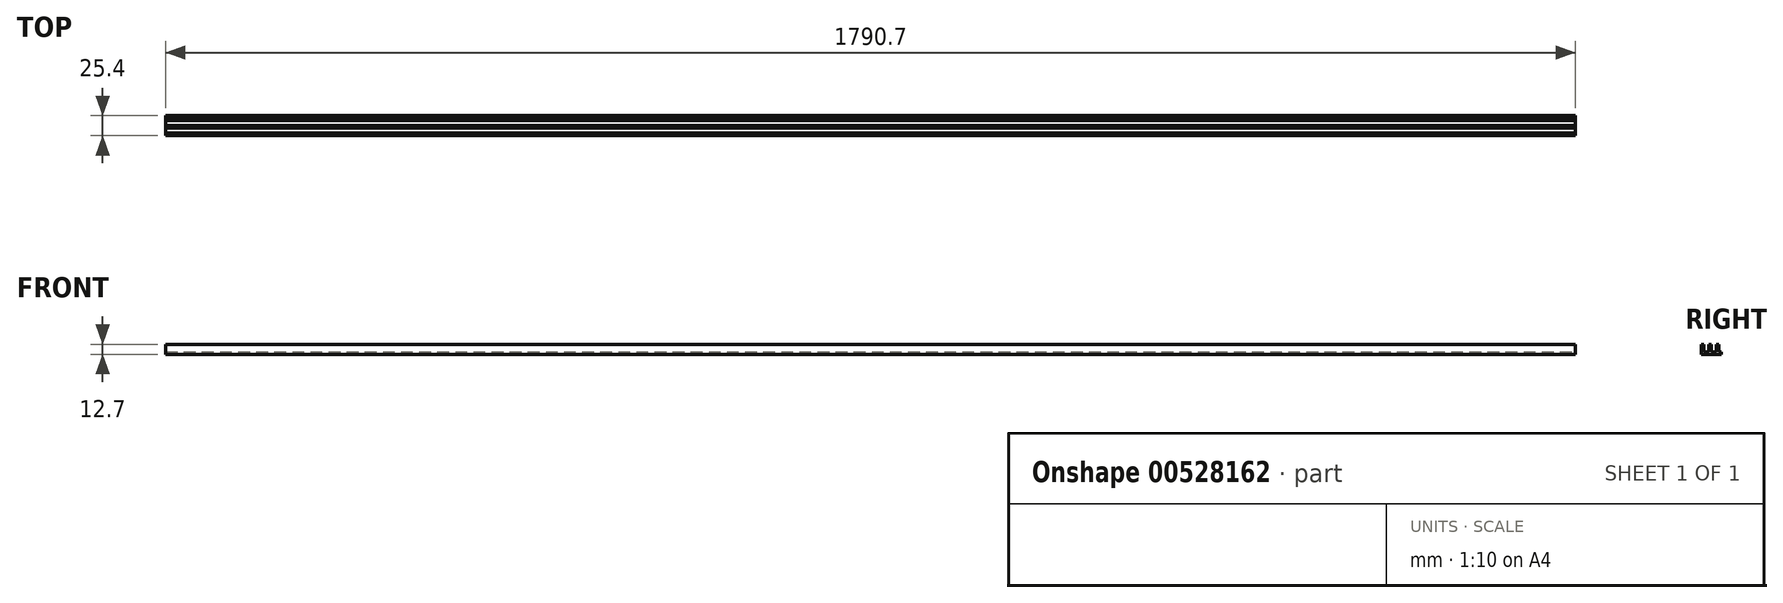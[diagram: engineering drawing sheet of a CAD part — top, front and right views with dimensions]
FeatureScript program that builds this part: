
annotation { "Feature Type Name" : "Feature", "Feature Type Description" : "" }
export const myFeature = defineFeature(function(context is Context, id is Id, definition is map)
    precondition{}
    {
        {
            var Q0;
            Q0=qCreatedBy(makeId("Top.planeOp"),FACE);
            var sketch = newSketch(context, id + "F0", { "sketchPlane" : qUnion([Q0])});
            skLineSegment(sketch, "E0.bottom", {"start": v(895.35, -12.7) * mm, "end": v(-895.35, -12.7) * mm});
            skLineSegment(sketch, "E0.top", {"start": v(895.35, 12.7) * mm, "end": v(-895.35, 12.7) * mm});
            skLineSegment(sketch, "E0.left", {"start": v(895.35, -12.7) * mm, "end": v(895.35, 12.7) * mm});
            skLineSegment(sketch, "E0.right", {"start": v(-895.35, -12.7) * mm, "end": v(-895.35, 12.7) * mm});
            skPoint(sketch, "E0.middle", {"position": v(0, 0) * mm});
            skSolve(sketch);
        }
        {
            var Q0;
            Q0=makeQuery(id+"F0.imprint","IMPRINT",FACE,{"disambiguationData":[TD([[makeQuery(id+"F0.imprint","IMPRINT",EDGE,{"derivedFrom":sQuery(id+"F0.wireOp",EDGE,"E0.bottom")}),-1.0]])]});
            extrude(context, id + "F1", {"entities" : qUnion([Q0]), "depth" : 3.17 * mm, "offsetDistance" : 25.4 * mm});
        }
        {
            var Q0;
            Q0=makeQuery(id+"F1.opExtrude","CAP_FACE",FACE,{"disambiguationData":[OSD([sQuery(id+"F0.wireOp",EDGE,"E0.bottom"),sQuery(id+"F0.wireOp",EDGE,"E0.top"),sQuery(id+"F0.wireOp",EDGE,"E0.left"),sQuery(id+"F0.wireOp",EDGE,"E0.right")])],"isStart":false});
            var sketch = newSketch(context, id + "F2", { "sketchPlane" : qUnion([Q0])});
            skLineSegment(sketch, "E1", {"start": v(-895.35, -12.7) * mm, "end": v(-895.35, -9.53) * mm});
            skLineSegment(sketch, "E2", {"start": v(-895.35, -9.53) * mm, "end": v(895.35, -9.53) * mm});
            skLineSegment(sketch, "E3", {"start": v(-895.35, -9.53) * mm, "end": v(-895.35, -3.18) * mm});
            skLineSegment(sketch, "E4", {"start": v(-895.35, -3.18) * mm, "end": v(895.35, -3.18) * mm});
            skLineSegment(sketch, "E5", {"start": v(-895.35, -3.18) * mm, "end": v(-895.35, 0) * mm});
            skLineSegment(sketch, "E6", {"start": v(-895.35, 0) * mm, "end": v(895.35, 0) * mm});
            skSolve(sketch);
        }
        {
            var Q0;
            Q0=makeQuery(id+"F2.imprint","IMPRINT",FACE,{"disambiguationData":[TD([[makeQuery(id+"F2.imprint","IMPRINT",EDGE,{"derivedFrom":sQuery(id+"F2.wireOp",EDGE,"E1")}),-1.0]])]});
            var Q1;
            {var subQ0=sQuery(id+"F2.wireOp",EDGE,"E4");Q1=makeQuery(id+"F2.imprint","IMPRINT",FACE,{"disambiguationData":[TD([[makeQuery(id+"F2.imprint","IMPRINT",EDGE,{"derivedFrom":subQ0}),1.0]])]});}
            extrude(context, id + "F3", {"entities" : qUnion([Q0, Q1]), "operationType" : NewBodyOperationType.ADD, "depth" : 9.52 * mm, "offsetDistance" : 25.4 * mm});
        }
        {
            var Q0;
            {var subQ0=sQuery(id+"F0.wireOp",EDGE,"E0.right");var subQ1=sQuery(id+"F0.wireOp",EDGE,"E0.left");var subQ4=sQuery(id+"F0.wireOp",EDGE,"E0.top");var subQ5=sQuery(id+"F0.wireOp",EDGE,"E0.bottom");Q0=makeQuery(id+"F3.boolean.opBoolean","SPLIT",FACE,{"disambiguationData":[TD([makeQuery(id+"F1.opExtrude","SWEPT_FACE",FACE,{"disambiguationData":[OSD([subQ4])]})])],"derivedFrom":makeQuery(id+"F1.opExtrude","CAP_FACE",FACE,{"disambiguationData":[OSD([subQ5,subQ4,subQ1,subQ0])],"isStart":false})});}
            var sketch = newSketch(context, id + "F4", { "sketchPlane" : qUnion([Q0])});
            skLineSegment(sketch, "E7", {"start": v(-895.35, 0) * mm, "end": v(-895.35, 6.35) * mm});
            skLineSegment(sketch, "E8", {"start": v(-895.35, 6.35) * mm, "end": v(895.35, 6.35) * mm});
            skLineSegment(sketch, "E9", {"start": v(-895.35, 6.35) * mm, "end": v(-895.35, 9.52) * mm});
            skLineSegment(sketch, "E10", {"start": v(-895.35, 9.52) * mm, "end": v(895.35, 9.52) * mm});
            skSolve(sketch);
        }
        {
            var Q0;
            {var subQ0=sQuery(id+"F4.wireOp",EDGE,"E8");Q0=makeQuery(id+"F4.imprint","IMPRINT",FACE,{"disambiguationData":[TD([[makeQuery(id+"F4.imprint","IMPRINT",EDGE,{"derivedFrom":subQ0}),1.0]])]});}
            extrude(context, id + "F5", {"entities" : qUnion([Q0]), "operationType" : NewBodyOperationType.ADD, "depth" : 9.52 * mm, "offsetDistance" : 25.4 * mm});
        }
    });
